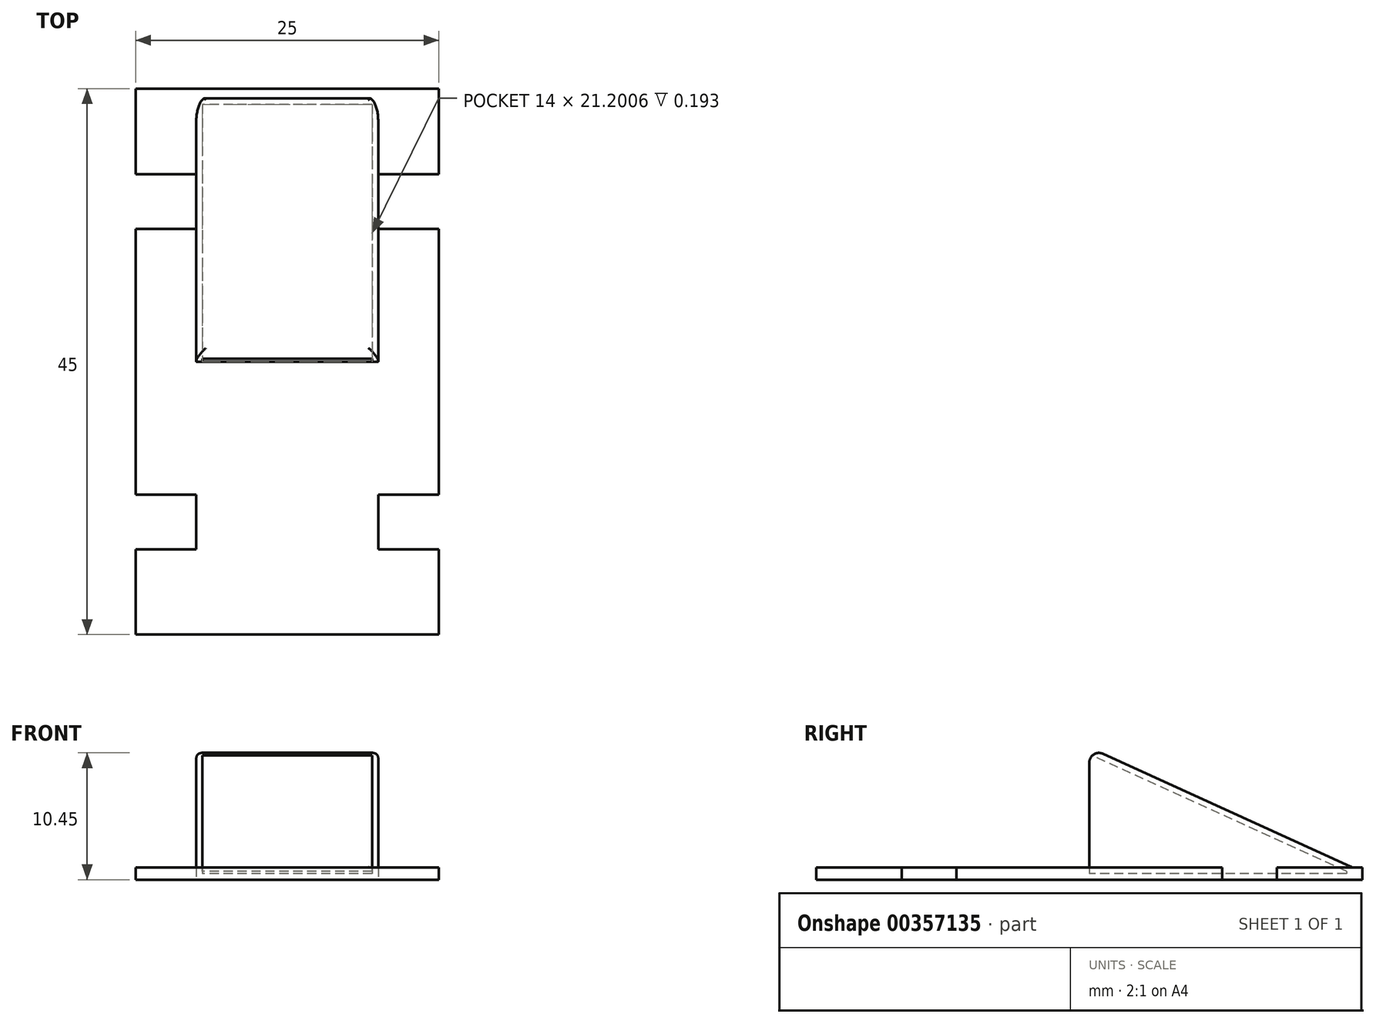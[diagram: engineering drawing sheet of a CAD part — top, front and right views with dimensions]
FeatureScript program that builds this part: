
annotation { "Feature Type Name" : "Feature", "Feature Type Description" : "" }
export const myFeature = defineFeature(function(context is Context, id is Id, definition is map)
    precondition{}
    {
        {
            var Q0;
            Q0=qCreatedBy(makeId("Top.planeOp"),FACE);
            var sketch = newSketch(context, id + "F0", { "sketchPlane" : qUnion([Q0])});
            skLineSegment(sketch, "E0.bottom", {"start": v(-12.5, -22.5) * mm, "end": v(12.5, -22.5) * mm});
            skLineSegment(sketch, "E0.top", {"start": v(-12.5, 22.5) * mm, "end": v(12.5, 22.5) * mm});
            skLineSegment(sketch, "E0.left", {"start": v(-12.5, -22.5) * mm, "end": v(-12.5, -15.46) * mm});
            skLineSegment(sketch, "E0.right", {"start": v(12.5, -22.5) * mm, "end": v(12.5, -15.46) * mm});
            skPoint(sketch, "E0.middle", {"position": v(0, 0) * mm});
            skLineSegment(sketch, "E1.bottom", {"start": v(-12.5, 15.46) * mm, "end": v(-7.5, 15.46) * mm});
            skLineSegment(sketch, "E1.top", {"start": v(-12.5, 10.96) * mm, "end": v(-7.5, 10.96) * mm});
            skLineSegment(sketch, "E1.right", {"start": v(-7.5, 15.46) * mm, "end": v(-7.5, 10.96) * mm});
            skLineSegment(sketch, "E2.MirrorCS", {"start": v(12.5, 15.46) * mm, "end": v(7.5, 15.46) * mm});
            skLineSegment(sketch, "E3.MirrorCS", {"start": v(7.5, 15.46) * mm, "end": v(7.5, 10.96) * mm});
            skLineSegment(sketch, "E4.MirrorCS", {"start": v(12.5, 10.96) * mm, "end": v(7.5, 10.96) * mm});
            skLineSegment(sketch, "E5.MirrorCS", {"start": v(12.5, -15.46) * mm, "end": v(7.5, -15.46) * mm});
            skLineSegment(sketch, "E6.MirrorCS", {"start": v(12.5, -10.96) * mm, "end": v(7.5, -10.96) * mm});
            skLineSegment(sketch, "E7.MirrorCS", {"start": v(7.5, -15.46) * mm, "end": v(7.5, -10.96) * mm});
            skLineSegment(sketch, "E8.MirrorCS", {"start": v(-7.5, -15.46) * mm, "end": v(-7.5, -10.96) * mm});
            skLineSegment(sketch, "E9.MirrorCS", {"start": v(-12.5, -10.96) * mm, "end": v(-7.5, -10.96) * mm});
            skLineSegment(sketch, "E10.MirrorCS", {"start": v(-12.5, -15.46) * mm, "end": v(-7.5, -15.46) * mm});
            skLineSegment(sketch, "E11.trimOffspring", {"start": v(12.5, 15.46) * mm, "end": v(12.5, 22.5) * mm});
            skLineSegment(sketch, "E12.trimOffspring", {"start": v(-12.5, 15.46) * mm, "end": v(-12.5, 22.5) * mm});
            skLineSegment(sketch, "E13.trimOffspring", {"start": v(-12.5, -10.96) * mm, "end": v(-12.5, 10.96) * mm});
            skLineSegment(sketch, "E14.trimOffspring", {"start": v(12.5, -10.96) * mm, "end": v(12.5, 10.96) * mm});
            skPoint(sketch, "E15.MirrorCS.end.orphan", {"position": v(-12.5, -10.96) * mm});
            skPoint(sketch, "E15.MirrorCS.start.orphan", {"position": v(-12.5, -15.46) * mm});
            skSolve(sketch);
        }
        {
            var Q0;
            {var subQ5=sQuery(id+"F0.wireOp",EDGE,"E0.bottom");Q0=makeQuery(id+"F0.imprint","IMPRINT",FACE,{"disambiguationData":[TD([[makeQuery(id+"F0.imprint","IMPRINT",EDGE,{"derivedFrom":subQ5}),1.0]])]});}
            extrude(context, id + "F1", {"entities" : qUnion([Q0]), "depth" : 1 * mm});
        }
        {
            var Q0;
            Q0=qCreatedBy(makeId("Right.planeOp"),FACE);
            var sketch = newSketch(context, id + "F2", { "sketchPlane" : qUnion([Q0])});
            skLineSegment(sketch, "E16", {"start": v(21.7, 1.01) * mm, "end": v(0, 10.9) * mm});
            skLineSegment(sketch, "E17", {"start": v(0, 10.9) * mm, "end": v(0, 0) * mm});
            skLineSegment(sketch, "E18", {"start": v(0, 0) * mm, "end": v(21.7, 0) * mm});
            skLineSegment(sketch, "E19", {"start": v(21.7, 1.01) * mm, "end": v(21.7, 0) * mm});
            skSolve(sketch);
        }
        {
            var Q0;
            Q0 = qSketchRegion(id + "F2", true);
            extrude(context, id + "F3", {"entities" : qUnion([Q0]), "operationType" : NewBodyOperationType.ADD, "endBound" : BoundingType.SYMMETRIC, "depth" : 15 * mm});
        }
        {
            var Q0;
            Q0=makeQuery(id+"F3.opExtrude","SWEPT_FACE",FACE,{"disambiguationData":[OSD([sQuery(id+"F2.wireOp",EDGE,"E17")])]});
            shell(context, id + "F4", {"entities" : qUnion([Q0]), "thickness" : 0.5 * mm});
        }
        {
            var Q0;
            Q0=makeQuery(id+"F3.opExtrude","SWEPT_FACE",FACE,{"disambiguationData":[OSD([sQuery(id+"F2.wireOp",EDGE,"E16")])]});
            fillet(context, id + "F5", {"entities" : qUnion([Q0]), "radius" : 0.8 * mm, "tangentPropagation" : true, "allowEdgeOverflow" : false});
        }
    });
